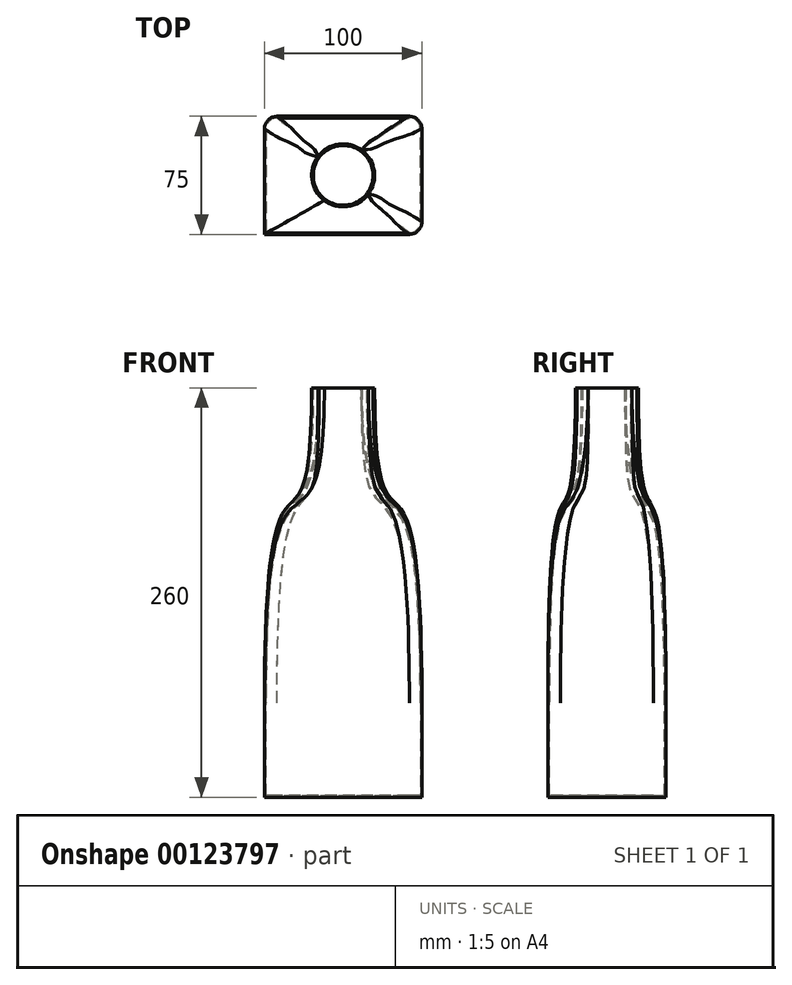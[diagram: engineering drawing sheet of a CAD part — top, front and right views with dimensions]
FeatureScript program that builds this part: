
annotation { "Feature Type Name" : "Feature", "Feature Type Description" : "" }
export const myFeature = defineFeature(function(context is Context, id is Id, definition is map)
    precondition{}
    {
        {
            var Q0;
            Q0=qCreatedBy(makeId("Top.planeOp"),FACE);
            var sketch = newSketch(context, id + "F0", { "sketchPlane" : qUnion([Q0])});
            skLineSegment(sketch, "E0.bottom", {"start": v(-50, 37.5) * mm, "end": v(50, 37.5) * mm});
            skLineSegment(sketch, "E0.top", {"start": v(-50, -37.5) * mm, "end": v(50, -37.5) * mm});
            skLineSegment(sketch, "E0.left", {"start": v(-50, 37.5) * mm, "end": v(-50, -37.5) * mm});
            skLineSegment(sketch, "E0.right", {"start": v(50, 37.5) * mm, "end": v(50, -37.5) * mm});
            skPoint(sketch, "E0.middle", {"position": v(0, 0) * mm});
            skSolve(sketch);
        }
        {
            var Q0;
            Q0=qCreatedBy(makeId("Top.planeOp"),FACE);
            cPlane(context, id + "F1", {"entities" : qUnion([Q0]), "cplaneType" : CPlaneType.OFFSET, "offset" : 200 * mm, "width" : 150 * mm, "height" : 150 * mm});
        }
        {
            var Q0;
            Q0=qCreatedBy(id+"F1.planeOp",FACE);
            var sketch = newSketch(context, id + "F2", { "sketchPlane" : qUnion([Q0])});
            skCircle(sketch, "E1", {"center": v(0, 0) * mm, "radius": 20 * mm});
            skSolve(sketch);
        }
        {
            var Q0;
            Q0=makeQuery(id+"F0.imprint","IMPRINT",FACE,{"disambiguationData":[TD([[makeQuery(id+"F0.imprint","IMPRINT",EDGE,{"derivedFrom":sQuery(id+"F0.wireOp",EDGE,"E0.bottom")}),-1.0]])]});
            var Q1;
            Q1=makeQuery(id+"F2.imprint","IMPRINT",FACE,{"disambiguationData":[TD([[makeQuery(id+"F2.imprint","IMPRINT",EDGE,{"derivedFrom":sQuery(id+"F2.wireOp",EDGE,"E1")}),1.0]])]});
            loft(context, id + "F3", {"startCondition" : LoftEndDerivativeType.NORMAL_TO_PROFILE, "startMagnitude" : 3, "endCondition" : LoftEndDerivativeType.NORMAL_TO_PROFILE, "endMagnitude" : 2, "sheetProfilesArray" : [{ "sheetProfileEntities" : qUnion([Q0]) }, { "sheetProfileEntities" : qUnion([Q1]) }]});
        }
        {
            var Q0;
            Q0=qCreatedBy(makeId("Top.planeOp"),FACE);
            var sketch = newSketch(context, id + "F4", { "sketchPlane" : qUnion([Q0])});
            skLineSegment(sketch, "E2.0", {"start": v(-50, -37.5) * mm, "end": v(50, -37.5) * mm});
            skLineSegment(sketch, "E3.0", {"start": v(50, -37.5) * mm, "end": v(50, 37.5) * mm});
            skLineSegment(sketch, "E4.0", {"start": v(50, 37.5) * mm, "end": v(-50, 37.5) * mm});
            skLineSegment(sketch, "E5.0", {"start": v(-50, 37.5) * mm, "end": v(-50, -37.5) * mm});
            skSolve(sketch);
        }
        {
            var Q0;
            Q0 = qSketchRegion(id + "F4", true);
            extrude(context, id + "F5", {"entities" : qUnion([Q0]), "operationType" : NewBodyOperationType.ADD, "oppositeDirection" : true, "depth" : 60 * mm});
        }
        {
            var Q0;
            Q0=makeQuery(id+"F3.opLoft","SWEPT_EDGE",EDGE,{"disambiguationData":[OSD([sQuery(id+"F0.wireOp",EDGE,"E0.bottom"),sQuery(id+"F0.wireOp",EDGE,"E0.top"),sQuery(id+"F0.wireOp",EDGE,"E0.right"),sQuery(id+"F2.wireOp",EDGE,"E1")])]});
            var Q1;
            Q1=makeQuery(id+"F3.opLoft","SWEPT_EDGE",EDGE,{"disambiguationData":[OSD([sQuery(id+"F0.wireOp",EDGE,"E0.bottom"),sQuery(id+"F0.wireOp",EDGE,"E0.left")])]});
            var Q2;
            Q2=makeQuery(id+"F3.opLoft","SWEPT_EDGE",EDGE,{"disambiguationData":[OSD([sQuery(id+"F0.wireOp",EDGE,"E0.bottom"),sQuery(id+"F0.wireOp",EDGE,"E0.top"),sQuery(id+"F0.wireOp",EDGE,"E0.left"),sQuery(id+"F2.wireOp",EDGE,"E1")])]});
            var Q3;
            Q3=makeQuery(id+"F3.opLoft","SWEPT_EDGE",EDGE,{"disambiguationData":[OSD([sQuery(id+"F0.wireOp",EDGE,"E0.top"),sQuery(id+"F0.wireOp",EDGE,"E0.left"),sQuery(id+"F0.wireOp",EDGE,"E0.right"),sQuery(id+"F2.wireOp",EDGE,"E1")])]});
            fillet(context, id + "F6", {"entities" : qUnion([Q0, Q1, Q2, Q3]), "radius" : 8 * mm, "tangentPropagation" : true, "allowEdgeOverflow" : false});
        }
        {
            var Q0;
            Q0=makeQuery(id+"F3.opLoft","CAP_FACE",FACE,{"disambiguationData":[OSD([makeQuery(id+"F2.imprint","IMPRINT",FACE,{"disambiguationData":[TD([[makeQuery(id+"F2.imprint","IMPRINT",EDGE,{"derivedFrom":sQuery(id+"F2.wireOp",EDGE,"E1")}),1.0]])]})])],"isStart":true});
            shell(context, id + "F7", {"entities" : qUnion([Q0]), "thickness" : 1 * mm});
        }
    });
